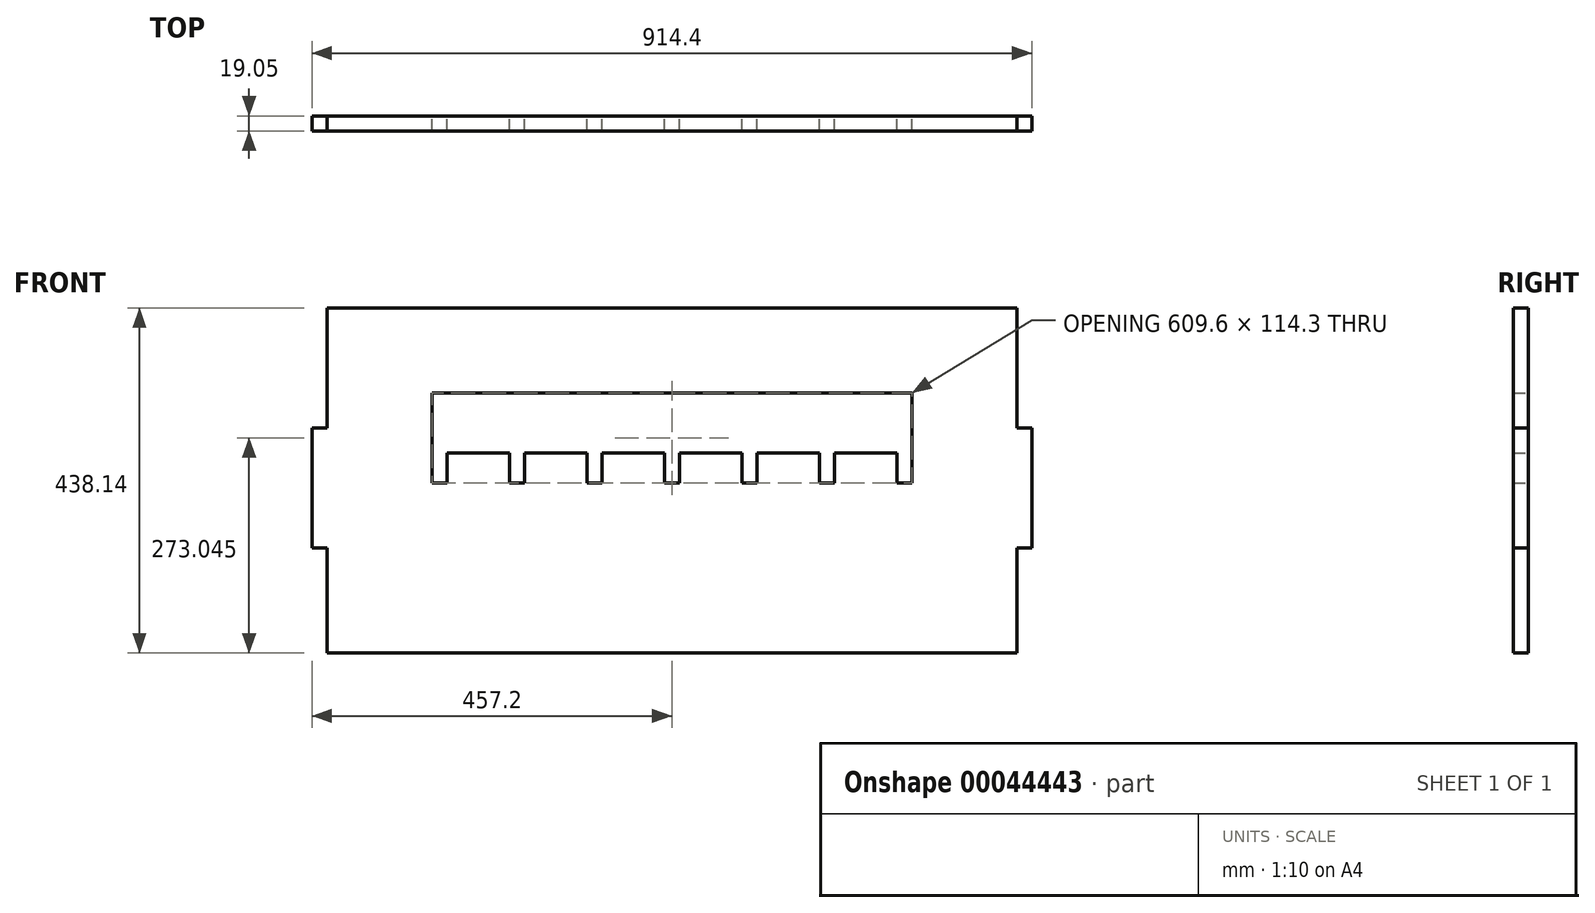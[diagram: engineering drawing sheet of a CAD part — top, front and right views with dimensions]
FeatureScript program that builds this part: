
annotation { "Feature Type Name" : "Feature", "Feature Type Description" : "" }
export const myFeature = defineFeature(function(context is Context, id is Id, definition is map)
    precondition{}
    {
        {
            var Q0;
            Q0=qCreatedBy(makeId("Front.planeOp"),FACE);
            var sketch = newSketch(context, id + "F0", { "sketchPlane" : qUnion([Q0])});
            skLineSegment(sketch, "E0.rect.bottom", {"start": v(-438.15, 219.08) * mm, "end": v(438.15, 219.08) * mm});
            skLineSegment(sketch, "E0.rect.top", {"start": v(-438.15, -219.08) * mm, "end": v(438.15, -219.08) * mm});
            skLineSegment(sketch, "E0.rect.left", {"start": v(-438.15, 219.08) * mm, "end": v(-438.15, -219.08) * mm});
            skLineSegment(sketch, "E0.rect.right", {"start": v(438.15, 219.08) * mm, "end": v(438.15, -219.08) * mm});
            skPoint(sketch, "E0.rect.middle", {"position": v(0, 0) * mm});
            skLineSegment(sketch, "E1.bottom", {"start": v(-438.15, 66.68) * mm, "end": v(-457.2, 66.68) * mm});
            skLineSegment(sketch, "E1.top", {"start": v(-438.15, -85.73) * mm, "end": v(-457.2, -85.73) * mm});
            skLineSegment(sketch, "E1.left", {"start": v(-438.15, 66.68) * mm, "end": v(-438.15, -85.72) * mm});
            skLineSegment(sketch, "E1.right", {"start": v(-457.2, 66.68) * mm, "end": v(-457.2, -85.73) * mm});
            skLineSegment(sketch, "E2.MirrorCS", {"start": v(438.15, -85.72) * mm, "end": v(457.2, -85.72) * mm});
            skLineSegment(sketch, "E3.MirrorCS", {"start": v(438.15, 66.68) * mm, "end": v(457.2, 66.68) * mm});
            skLineSegment(sketch, "E4.MirrorCS", {"start": v(457.2, 66.68) * mm, "end": v(457.2, -85.73) * mm});
            skLineSegment(sketch, "E5.MirrorCS", {"start": v(438.15, 66.68) * mm, "end": v(438.15, -85.72) * mm});
            skLineSegment(sketch, "E6.bottom", {"start": v(-152.4, -219.07) * mm, "end": v(152.4, -219.07) * mm});
            skLineSegment(sketch, "E6.top", {"start": v(-152.4, -257.17) * mm, "end": v(152.4, -257.17) * mm});
            skLineSegment(sketch, "E6.left", {"start": v(-152.4, -219.08) * mm, "end": v(-152.4, -257.17) * mm});
            skLineSegment(sketch, "E6.right", {"start": v(152.4, -219.07) * mm, "end": v(152.4, -257.17) * mm});
            skLineSegment(sketch, "E7.right", {"start": v(304.8, 111.12) * mm, "end": v(304.8, 34.92) * mm});
            skLineSegment(sketch, "E7.left", {"start": v(-304.8, 111.12) * mm, "end": v(-304.8, 34.92) * mm});
            skLineSegment(sketch, "E7.top", {"start": v(-304.8, 34.92) * mm, "end": v(304.8, 34.92) * mm});
            skLineSegment(sketch, "E7.bottom", {"start": v(-304.8, 111.12) * mm, "end": v(304.8, 111.12) * mm});
            skLineSegment(sketch, "E8.bottom", {"start": v(88.9, 34.93) * mm, "end": v(107.95, 34.93) * mm});
            skLineSegment(sketch, "E9.right", {"start": v(9.52, 34.93) * mm, "end": v(9.52, -3.17) * mm});
            skLineSegment(sketch, "E9.top", {"start": v(-9.53, -3.17) * mm, "end": v(9.53, -3.17) * mm});
            skLineSegment(sketch, "E10.right", {"start": v(-187.32, 34.93) * mm, "end": v(-187.32, -3.17) * mm});
            skLineSegment(sketch, "E11.right", {"start": v(206.38, 34.93) * mm, "end": v(206.38, -3.17) * mm});
            skLineSegment(sketch, "E12.right", {"start": v(-88.9, 34.93) * mm, "end": v(-88.9, -3.17) * mm});
            skLineSegment(sketch, "E9.left", {"start": v(-9.53, 34.92) * mm, "end": v(-9.53, -3.17) * mm});
            skLineSegment(sketch, "E12.bottom", {"start": v(-107.95, 34.93) * mm, "end": v(-88.9, 34.93) * mm});
            skLineSegment(sketch, "E8.top", {"start": v(88.9, -3.17) * mm, "end": v(107.95, -3.17) * mm});
            skLineSegment(sketch, "E11.top", {"start": v(187.32, -3.17) * mm, "end": v(206.37, -3.17) * mm});
            skLineSegment(sketch, "E10.top", {"start": v(-206.38, -3.17) * mm, "end": v(-187.33, -3.17) * mm});
            skLineSegment(sketch, "E11.left", {"start": v(187.32, 34.92) * mm, "end": v(187.32, -3.17) * mm});
            skLineSegment(sketch, "E12.top", {"start": v(-107.95, -3.17) * mm, "end": v(-88.9, -3.17) * mm});
            skLineSegment(sketch, "E8.left", {"start": v(88.9, 34.92) * mm, "end": v(88.9, -3.17) * mm});
            skLineSegment(sketch, "E10.left", {"start": v(-206.37, 34.92) * mm, "end": v(-206.37, -3.17) * mm});
            skLineSegment(sketch, "E11.bottom", {"start": v(187.32, 34.93) * mm, "end": v(206.37, 34.93) * mm});
            skLineSegment(sketch, "E10.bottom", {"start": v(-206.38, 34.93) * mm, "end": v(-187.33, 34.93) * mm});
            skLineSegment(sketch, "E8.right", {"start": v(107.95, 34.93) * mm, "end": v(107.95, -3.17) * mm});
            skLineSegment(sketch, "E12.left", {"start": v(-107.95, 34.92) * mm, "end": v(-107.95, -3.17) * mm});
            skLineSegment(sketch, "E9.bottom", {"start": v(-9.53, 34.93) * mm, "end": v(9.53, 34.93) * mm});
            skLineSegment(sketch, "E13", {"start": v(-304.8, 34.92) * mm, "end": v(-304.8, -3.17) * mm});
            skLineSegment(sketch, "E14", {"start": v(-304.8, -3.17) * mm, "end": v(-285.75, -3.17) * mm});
            skLineSegment(sketch, "E15", {"start": v(-285.75, -3.17) * mm, "end": v(-285.75, 34.92) * mm});
            skLineSegment(sketch, "E16.bottom", {"start": v(304.8, 34.92) * mm, "end": v(285.75, 34.92) * mm});
            skLineSegment(sketch, "E16.top", {"start": v(304.8, -3.17) * mm, "end": v(285.75, -3.17) * mm});
            skLineSegment(sketch, "E16.left", {"start": v(304.8, 34.92) * mm, "end": v(304.8, -3.17) * mm});
            skLineSegment(sketch, "E16.right", {"start": v(285.75, 34.92) * mm, "end": v(285.75, -3.17) * mm});
            skSolve(sketch);
        }
        {
            var Q0;
            {var subQ39=sQuery(id+"F0.wireOp",EDGE,"E0.rect.bottom");Q0=makeQuery(id+"F0.imprint","IMPRINT",FACE,{"disambiguationData":[TD([[makeQuery(id+"F0.imprint","IMPRINT",EDGE,{"derivedFrom":subQ39}),-1.0]])]});}
            var Q1;
            Q1=makeQuery(id+"F0.imprint","IMPRINT",FACE,{"disambiguationData":[TD([[makeQuery(id+"F0.imprint","IMPRINT",EDGE,{"derivedFrom":sQuery(id+"F0.wireOp",EDGE,"E1.bottom")}),1.0]])]});
            var Q2;
            Q2=makeQuery(id+"F0.imprint","IMPRINT",FACE,{"disambiguationData":[TD([[makeQuery(id+"F0.imprint","IMPRINT",EDGE,{"derivedFrom":sQuery(id+"F0.wireOp",EDGE,"E6.bottom")}),-1.0]])]});
            var Q3;
            Q3=makeQuery(id+"F0.imprint","IMPRINT",FACE,{"disambiguationData":[TD([[makeQuery(id+"F0.imprint","IMPRINT",EDGE,{"derivedFrom":sQuery(id+"F0.wireOp",EDGE,"E2.MirrorCS")}),1.0]])]});
            var Q4;
            Q4=makeQuery(id+"F0.imprint","IMPRINT",FACE,{"disambiguationData":[TD([[makeQuery(id+"F0.imprint","IMPRINT",EDGE,{"derivedFrom":sQuery(id+"F0.wireOp",EDGE,"8aa589df-ecd3-4c38-be28-ef09b16f95c7.bottom")}),-1.0]])]});
            extrude(context, id + "F1", {"entities" : qUnion([Q0, Q1, Q2, Q3, Q4]), "depth" : 19.05 * mm});
        }
    });
